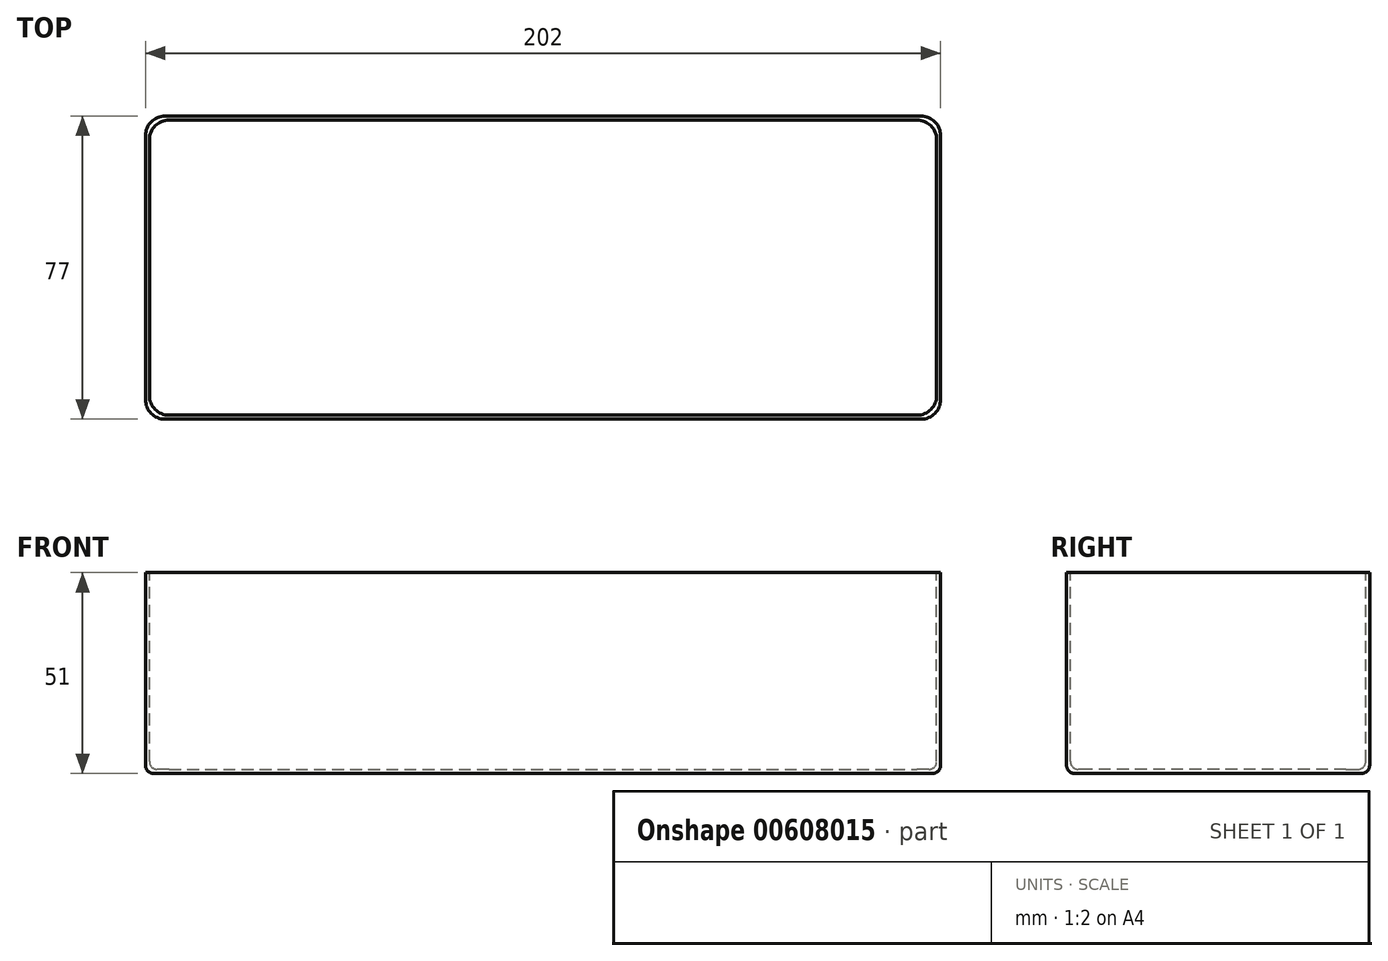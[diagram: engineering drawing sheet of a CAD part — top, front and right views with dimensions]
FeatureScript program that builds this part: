
annotation { "Feature Type Name" : "Feature", "Feature Type Description" : "" }
export const myFeature = defineFeature(function(context is Context, id is Id, definition is map)
    precondition{}
    {
        {
            var Q0;
            Q0=qCreatedBy(makeId("Top.planeOp"),FACE);
            var sketch = newSketch(context, id + "F0", { "sketchPlane" : qUnion([Q0])});
            skLineSegment(sketch, "E0.bottom", {"start": v(-103.81, 37.14) * mm, "end": v(98.19, 37.14) * mm});
            skLineSegment(sketch, "E0.top", {"start": v(-103.81, -39.86) * mm, "end": v(98.19, -39.86) * mm});
            skLineSegment(sketch, "E0.left", {"start": v(-103.81, 37.14) * mm, "end": v(-103.81, -39.86) * mm});
            skLineSegment(sketch, "E0.right", {"start": v(98.19, 37.14) * mm, "end": v(98.19, -39.86) * mm});
            skSolve(sketch);
        }
        {
            var Q0;
            Q0=makeQuery(id+"F0.imprint","IMPRINT",FACE,{"disambiguationData":[TD([[makeQuery(id+"F0.imprint","IMPRINT",EDGE,{"derivedFrom":sQuery(id+"F0.wireOp",EDGE,"E0.bottom")}),-1.0]])]});
            extrude(context, id + "F1", {"entities" : qUnion([Q0]), "depth" : 51 * mm, "offsetDistance" : 25 * mm});
        }
        {
            var Q0;
            Q0=makeQuery(id+"F1.opExtrude","CAP_FACE",FACE,{"disambiguationData":[OSD([sQuery(id+"F0.wireOp",EDGE,"E0.bottom"),sQuery(id+"F0.wireOp",EDGE,"E0.top"),sQuery(id+"F0.wireOp",EDGE,"E0.left"),sQuery(id+"F0.wireOp",EDGE,"E0.right")])],"isStart":false});
            var sketch = newSketch(context, id + "F2", { "sketchPlane" : qUnion([Q0])});
            skLineSegment(sketch, "E1.bottom", {"start": v(-102.81, 36.14) * mm, "end": v(97.19, 36.14) * mm});
            skLineSegment(sketch, "E1.top", {"start": v(-102.81, -38.86) * mm, "end": v(97.19, -38.86) * mm});
            skLineSegment(sketch, "E1.left", {"start": v(-102.81, 36.14) * mm, "end": v(-102.81, -38.86) * mm});
            skLineSegment(sketch, "E1.right", {"start": v(97.19, 36.14) * mm, "end": v(97.19, -38.86) * mm});
            skPoint(sketch, "E1.middle", {"position": v(-2.81, -1.36) * mm});
            skPoint(sketch, "E1.middle.positionSnap0", {"position": v(-103.81, -1.36) * mm});
            skPoint(sketch, "E1.middle.positionSnap1", {"position": v(-2.81, 37.14) * mm});
            skPoint(sketch, "E1.centerSnap0", {"position": v(-103.81, -1.36) * mm});
            skPoint(sketch, "E1.centerSnap1", {"position": v(-2.81, 37.14) * mm});
            skSolve(sketch);
        }
        {
            var Q0;
            Q0=makeQuery(id+"F2.imprint","IMPRINT",FACE,{"disambiguationData":[TD([[makeQuery(id+"F2.imprint","IMPRINT",EDGE,{"derivedFrom":sQuery(id+"F2.wireOp",EDGE,"E1.bottom")}),-1.0]])]});
            extrude(context, id + "F3", {"entities" : qUnion([Q0]), "operationType" : NewBodyOperationType.REMOVE, "oppositeDirection" : true, "depth" : 50 * mm, "offsetDistance" : 25 * mm});
        }
        {
            var Q0;
            Q0=makeQuery(id+"F3.boolean.opBoolean","COPY",EDGE,{"derivedFrom":makeQuery(id+"F3.opExtrude","SWEPT_EDGE",EDGE,{"disambiguationData":[OSD([sQuery(id+"F2.wireOp",EDGE,"E1.bottom"),sQuery(id+"F2.wireOp",EDGE,"E1.right")])]})});
            var Q1;
            Q1=makeQuery(id+"F3.boolean.opBoolean","COPY",EDGE,{"derivedFrom":makeQuery(id+"F3.opExtrude","SWEPT_EDGE",EDGE,{"disambiguationData":[OSD([sQuery(id+"F2.wireOp",EDGE,"E1.bottom"),sQuery(id+"F2.wireOp",EDGE,"E1.left")])]})});
            var Q2;
            Q2=makeQuery(id+"F3.boolean.opBoolean","COPY",EDGE,{"derivedFrom":makeQuery(id+"F3.opExtrude","SWEPT_EDGE",EDGE,{"disambiguationData":[OSD([sQuery(id+"F2.wireOp",EDGE,"E1.top"),sQuery(id+"F2.wireOp",EDGE,"E1.right")])]})});
            var Q3;
            Q3=makeQuery(id+"F3.boolean.opBoolean","COPY",EDGE,{"derivedFrom":makeQuery(id+"F3.opExtrude","SWEPT_EDGE",EDGE,{"disambiguationData":[OSD([sQuery(id+"F2.wireOp",EDGE,"E1.top"),sQuery(id+"F2.wireOp",EDGE,"E1.left")])]})});
            var Q4;
            Q4=makeQuery(id+"F1.opExtrude","SWEPT_EDGE",EDGE,{"disambiguationData":[OSD([sQuery(id+"F0.wireOp",EDGE,"E0.bottom"),sQuery(id+"F0.wireOp",EDGE,"E0.right")])]});
            var Q5;
            Q5=makeQuery(id+"F1.opExtrude","SWEPT_EDGE",EDGE,{"disambiguationData":[OSD([sQuery(id+"F0.wireOp",EDGE,"E0.bottom"),sQuery(id+"F0.wireOp",EDGE,"E0.left")])]});
            var Q6;
            Q6=makeQuery(id+"F1.opExtrude","SWEPT_EDGE",EDGE,{"disambiguationData":[OSD([sQuery(id+"F0.wireOp",EDGE,"E0.top"),sQuery(id+"F0.wireOp",EDGE,"E0.right")])]});
            var Q7;
            Q7=makeQuery(id+"F1.opExtrude","SWEPT_EDGE",EDGE,{"disambiguationData":[OSD([sQuery(id+"F0.wireOp",EDGE,"E0.top"),sQuery(id+"F0.wireOp",EDGE,"E0.left")])]});
            fillet(context, id + "F4", {"entities" : qUnion([Q0, Q1, Q2, Q3, Q4, Q5, Q6, Q7]), "radius" : 5 * mm, "tangentPropagation" : true, "allowEdgeOverflow" : false});
        }
        {
            var Q0;
            Q0=makeQuery(id+"F3.boolean.opBoolean","COPY",EDGE,{"derivedFrom":makeQuery(id+"F3.opExtrude","CAP_EDGE",EDGE,{"disambiguationData":[OSD([sQuery(id+"F2.wireOp",EDGE,"E1.right")])],"isStart":false})});
            var Q1;
            {var subQ0=sQuery(id+"F2.wireOp",EDGE,"E1.right");var subQ1=sQuery(id+"F2.wireOp",EDGE,"E1.bottom");Q1=makeQuery(id+"F4.opFillet","BLEND_EDGE",EDGE,{"blendedFrom":[makeQuery(id+"F3.boolean.opBoolean","COPY",EDGE,{"derivedFrom":makeQuery(id+"F3.opExtrude","SWEPT_EDGE",EDGE,{"disambiguationData":[OSD([subQ1,subQ0])]})}),makeQuery(id+"F3.boolean.opBoolean","COPY",FACE,{"derivedFrom":makeQuery(id+"F3.opExtrude","CAP_FACE",FACE,{"disambiguationData":[OSD([subQ1,sQuery(id+"F2.wireOp",EDGE,"E1.top"),sQuery(id+"F2.wireOp",EDGE,"E1.left"),subQ0])],"isStart":false})})],"blendedInto":[makeQuery(id+"F3.boolean.opBoolean","COPY",FACE,{"derivedFrom":makeQuery(id+"F3.opExtrude","CAP_FACE",FACE,{"disambiguationData":[OSD([subQ1,sQuery(id+"F2.wireOp",EDGE,"E1.top"),sQuery(id+"F2.wireOp",EDGE,"E1.left"),subQ0])],"isStart":false})})]});}
            var Q2;
            Q2=makeQuery(id+"F3.boolean.opBoolean","COPY",EDGE,{"derivedFrom":makeQuery(id+"F3.opExtrude","CAP_EDGE",EDGE,{"disambiguationData":[OSD([sQuery(id+"F2.wireOp",EDGE,"E1.bottom")])],"isStart":false})});
            var Q3;
            {var subQ0=sQuery(id+"F2.wireOp",EDGE,"E1.left");var subQ1=sQuery(id+"F2.wireOp",EDGE,"E1.bottom");Q3=makeQuery(id+"F4.opFillet","BLEND_EDGE",EDGE,{"blendedFrom":[makeQuery(id+"F3.boolean.opBoolean","COPY",EDGE,{"derivedFrom":makeQuery(id+"F3.opExtrude","SWEPT_EDGE",EDGE,{"disambiguationData":[OSD([subQ1,subQ0])]})}),makeQuery(id+"F3.boolean.opBoolean","COPY",FACE,{"derivedFrom":makeQuery(id+"F3.opExtrude","CAP_FACE",FACE,{"disambiguationData":[OSD([subQ1,sQuery(id+"F2.wireOp",EDGE,"E1.top"),subQ0,sQuery(id+"F2.wireOp",EDGE,"E1.right")])],"isStart":false})})],"blendedInto":[makeQuery(id+"F3.boolean.opBoolean","COPY",FACE,{"derivedFrom":makeQuery(id+"F3.opExtrude","CAP_FACE",FACE,{"disambiguationData":[OSD([subQ1,sQuery(id+"F2.wireOp",EDGE,"E1.top"),subQ0,sQuery(id+"F2.wireOp",EDGE,"E1.right")])],"isStart":false})})]});}
            var Q4;
            Q4=makeQuery(id+"F3.boolean.opBoolean","COPY",EDGE,{"derivedFrom":makeQuery(id+"F3.opExtrude","CAP_EDGE",EDGE,{"disambiguationData":[OSD([sQuery(id+"F2.wireOp",EDGE,"E1.top")])],"isStart":false})});
            var Q5;
            {var subQ0=sQuery(id+"F2.wireOp",EDGE,"E1.right");var subQ1=sQuery(id+"F2.wireOp",EDGE,"E1.top");Q5=makeQuery(id+"F4.opFillet","BLEND_EDGE",EDGE,{"blendedFrom":[makeQuery(id+"F3.boolean.opBoolean","COPY",EDGE,{"derivedFrom":makeQuery(id+"F3.opExtrude","SWEPT_EDGE",EDGE,{"disambiguationData":[OSD([subQ1,subQ0])]})}),makeQuery(id+"F3.boolean.opBoolean","COPY",FACE,{"derivedFrom":makeQuery(id+"F3.opExtrude","CAP_FACE",FACE,{"disambiguationData":[OSD([sQuery(id+"F2.wireOp",EDGE,"E1.bottom"),subQ1,sQuery(id+"F2.wireOp",EDGE,"E1.left"),subQ0])],"isStart":false})})],"blendedInto":[makeQuery(id+"F3.boolean.opBoolean","COPY",FACE,{"derivedFrom":makeQuery(id+"F3.opExtrude","CAP_FACE",FACE,{"disambiguationData":[OSD([sQuery(id+"F2.wireOp",EDGE,"E1.bottom"),subQ1,sQuery(id+"F2.wireOp",EDGE,"E1.left"),subQ0])],"isStart":false})})]});}
            fillet(context, id + "F5", {"entities" : qUnion([Q0, Q1, Q2, Q3, Q4, Q5]), "radius" : 2 * mm, "tangentPropagation" : true, "allowEdgeOverflow" : false});
        }
        {
            var Q0;
            Q0=makeQuery(id+"F1.opExtrude","CAP_FACE",FACE,{"disambiguationData":[OSD([sQuery(id+"F0.wireOp",EDGE,"E0.bottom"),sQuery(id+"F0.wireOp",EDGE,"E0.top"),sQuery(id+"F0.wireOp",EDGE,"E0.left"),sQuery(id+"F0.wireOp",EDGE,"E0.right")])],"isStart":true});
            fillet(context, id + "F6", {"entities" : qUnion([Q0]), "radius" : 2 * mm, "tangentPropagation" : true, "allowEdgeOverflow" : false});
        }
    });
